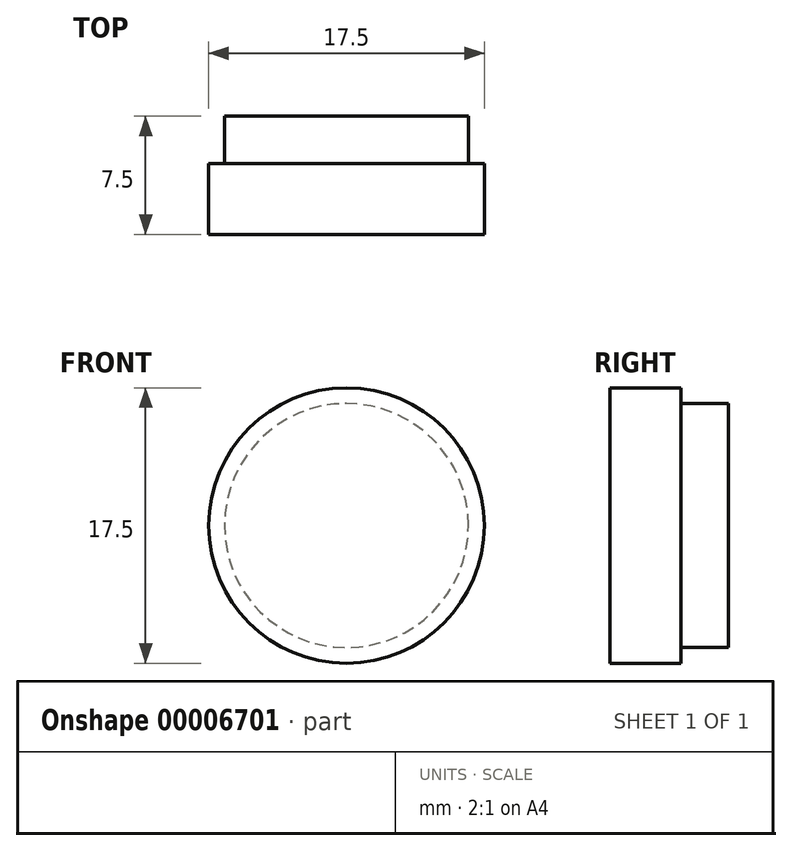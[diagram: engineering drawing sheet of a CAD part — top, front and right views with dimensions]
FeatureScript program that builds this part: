
annotation { "Feature Type Name" : "Feature", "Feature Type Description" : "" }
export const myFeature = defineFeature(function(context is Context, id is Id, definition is map)
    precondition{}
    {
        {
            var Q0;
            Q0=qCreatedBy(makeId("Right.planeOp"),FACE);
            var sketch = newSketch(context, id + "F0", { "sketchPlane" : qUnion([Q0])});
            skLineSegment(sketch, "E0", {"start": v(0, 0) * mm, "end": v(0, 8.75) * mm});
            skLineSegment(sketch, "E1", {"start": v(0, 8.75) * mm, "end": v(4.5, 8.75) * mm});
            skLineSegment(sketch, "E2", {"start": v(4.5, 8.75) * mm, "end": v(4.5, 7.75) * mm});
            skLineSegment(sketch, "E3", {"start": v(4.5, 7.75) * mm, "end": v(7.5, 7.75) * mm});
            skLineSegment(sketch, "E4", {"start": v(7.5, 7.75) * mm, "end": v(7.5, 0) * mm});
            skLineSegment(sketch, "E5", {"start": v(7.5, 0) * mm, "end": v(0, 0) * mm});
            skSolve(sketch);
        }
        {
            var Q0;
            Q0=makeQuery(id+"F0.imprint","IMPRINT",FACE,{"disambiguationData":[TD([[makeQuery(id+"F0.imprint","IMPRINT",EDGE,{"derivedFrom":sQuery(id+"F0.wireOp",EDGE,"E0")}),-1.0]])]});
            var Q1;
            Q1=sQuery(id+"F0.wireOp",EDGE,"E5");
            revolve(context, id + "F1", {"entities" : qUnion([Q0]), "axis" : qUnion([Q1]), "revolveType" : RevolveType.FULL});
        }
    });
